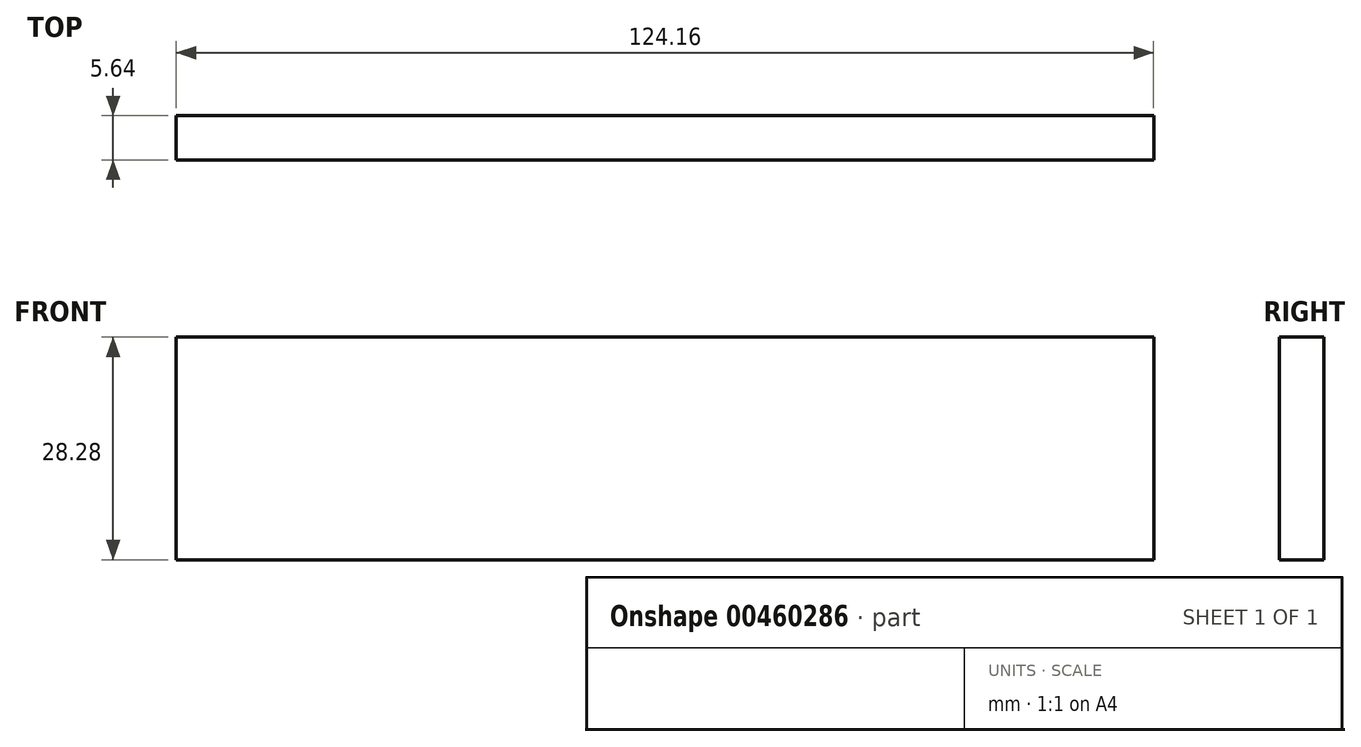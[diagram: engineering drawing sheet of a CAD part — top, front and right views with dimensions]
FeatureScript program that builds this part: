
annotation { "Feature Type Name" : "Feature", "Feature Type Description" : "" }
export const myFeature = defineFeature(function(context is Context, id is Id, definition is map)
    precondition{}
    {
        {
            var Q0;
            Q0=qCreatedBy(makeId("Front.planeOp"),FACE);
            var sketch = newSketch(context, id + "F0", { "sketchPlane" : qUnion([Q0])});
            skLineSegment(sketch, "E0.bottom", {"start": v(-62.08, 14.14) * mm, "end": v(62.08, 14.14) * mm});
            skLineSegment(sketch, "E0.top", {"start": v(-62.08, -14.14) * mm, "end": v(62.08, -14.14) * mm});
            skLineSegment(sketch, "E0.left", {"start": v(-62.08, 14.14) * mm, "end": v(-62.08, -14.14) * mm});
            skLineSegment(sketch, "E0.right", {"start": v(62.08, 14.14) * mm, "end": v(62.08, -14.14) * mm});
            skPoint(sketch, "E0.middle", {"position": v(0, 0) * mm});
            skSolve(sketch);
        }
        {
            var Q0;
            Q0 = qSketchRegion(id + "F0", true);
            extrude(context, id + "F1", {"entities" : qUnion([Q0]), "depth" : 5.64 * mm});
        }
    });
